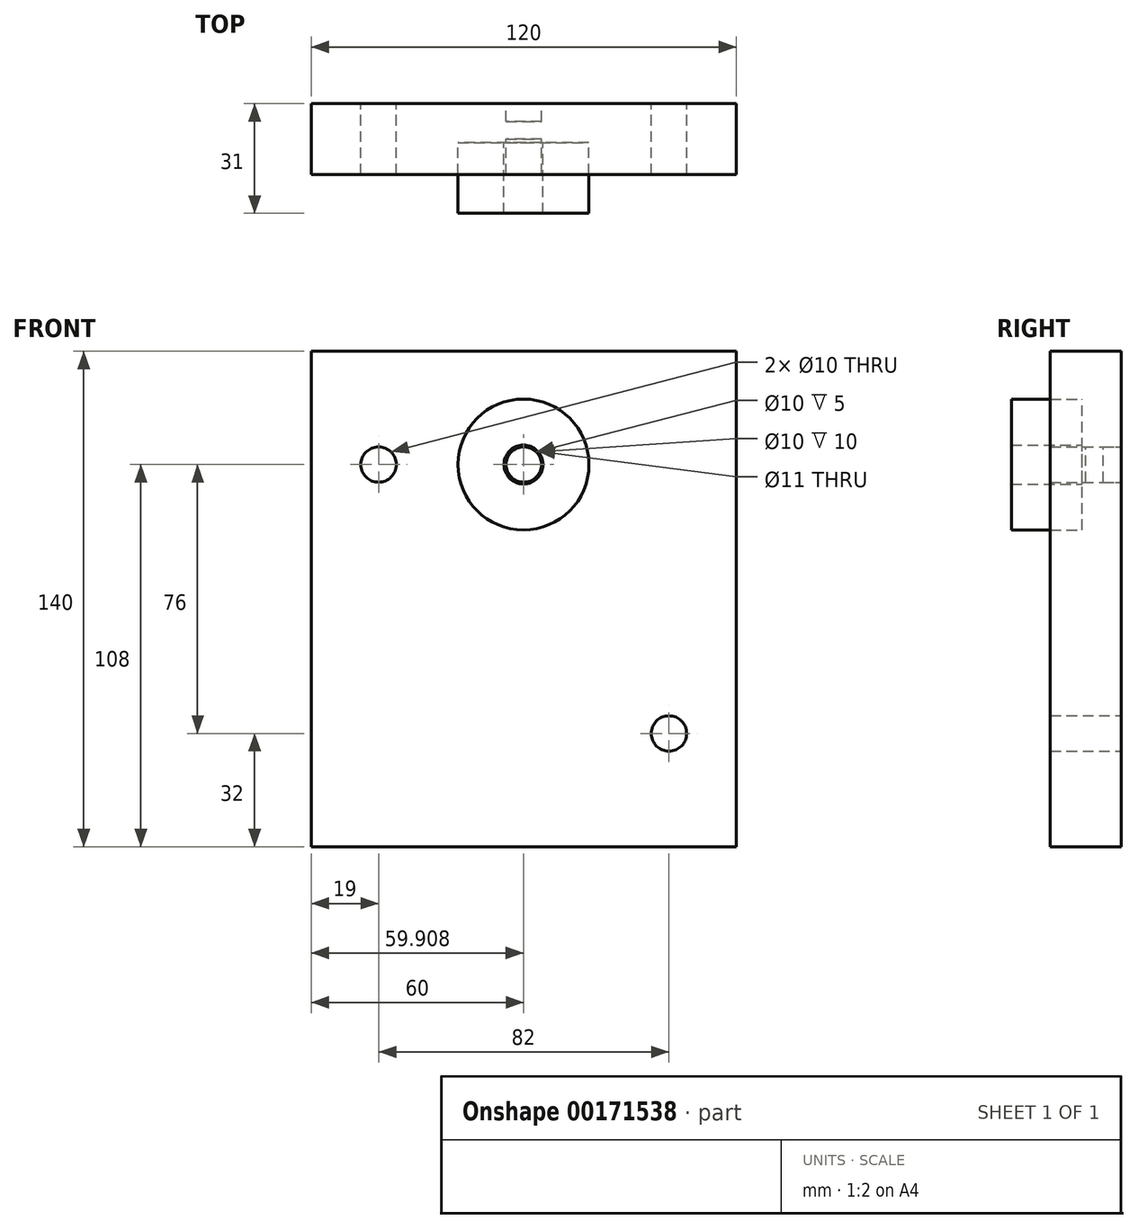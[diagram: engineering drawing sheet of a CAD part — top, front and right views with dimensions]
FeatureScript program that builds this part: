
annotation { "Feature Type Name" : "Feature", "Feature Type Description" : "" }
export const myFeature = defineFeature(function(context is Context, id is Id, definition is map)
    precondition{}
    {
        {
            var Q0;
            Q0=qCreatedBy(makeId("Front.planeOp"),FACE);
            var sketch = newSketch(context, id + "F0", { "sketchPlane" : qUnion([Q0])});
            skLineSegment(sketch, "E0.bottom", {"start": v(60, 70) * mm, "end": v(-60, 70) * mm});
            skLineSegment(sketch, "E0.top", {"start": v(60, -70) * mm, "end": v(-60, -70) * mm});
            skLineSegment(sketch, "E0.left", {"start": v(60, 70) * mm, "end": v(60, -70) * mm});
            skLineSegment(sketch, "E0.right", {"start": v(-60, 70) * mm, "end": v(-60, -70) * mm});
            skPoint(sketch, "E0.middle", {"position": v(0, 0) * mm});
            skLineSegment(sketch, "E1.bottom", {"start": v(60, 19) * mm, "end": v(-60, 19) * mm, "construction": true});
            skLineSegment(sketch, "E1.top", {"start": v(60, -19) * mm, "end": v(-60, -19) * mm, "construction": true});
            skLineSegment(sketch, "E1.left", {"start": v(60, 19) * mm, "end": v(60, -19) * mm, "construction": true});
            skLineSegment(sketch, "E1.right", {"start": v(-60, 17.79) * mm, "end": v(-60, -19) * mm, "construction": true});
            skCircle(sketch, "E2", {"center": v(0, 38) * mm, "radius": 5 * mm});
            skCircle(sketch, "E3", {"center": v(0, -38) * mm, "radius": 5 * mm});
            skCircle(sketch, "E4", {"center": v(0, 38) * mm, "radius": 19 * mm, "construction": true});
            skCircle(sketch, "E5", {"center": v(41, 38) * mm, "radius": 5 * mm});
            skCircle(sketch, "E6.0", {"center": v(41, 38) * mm, "radius": 19 * mm, "construction": true});
            skCircle(sketch, "E7.MirrorC", {"center": v(41, -38) * mm, "radius": 5 * mm});
            skCircle(sketch, "E8.MirrorC", {"center": v(41, -38) * mm, "radius": 19 * mm, "construction": true});
            skCircle(sketch, "E9.MirrorC", {"center": v(-41, 38) * mm, "radius": 5 * mm});
            skCircle(sketch, "E10.MirrorC", {"center": v(-41, 38) * mm, "radius": 19 * mm, "construction": true});
            skCircle(sketch, "E11.MirrorC", {"center": v(-41, -38) * mm, "radius": 5 * mm});
            skCircle(sketch, "E12.MirrorC", {"center": v(-41, -38) * mm, "radius": 19 * mm, "construction": true});
            skSolve(sketch);
        }
        {
            var Q0;
            Q0=qSketchRegion(id+"F0",true);
            var Q1;
            Q1=makeQuery(id+"F0.imprint","IMPRINT",FACE,{"disambiguationData":[TD([[makeQuery(id+"F0.imprint","IMPRINT",EDGE,{"derivedFrom":sQuery(id+"F0.wireOp",EDGE,"E2")}),1.0]])]});
            var Q2;
            Q2=makeQuery(id+"F0.imprint","IMPRINT",FACE,{"disambiguationData":[TD([[makeQuery(id+"F0.imprint","IMPRINT",EDGE,{"derivedFrom":sQuery(id+"F0.wireOp",EDGE,"E9.MirrorC")}),-1.0]])]});
            var Q3;
            Q3=makeQuery(id+"F0.imprint","IMPRINT",FACE,{"disambiguationData":[TD([[makeQuery(id+"F0.imprint","IMPRINT",EDGE,{"derivedFrom":sQuery(id+"F0.wireOp",EDGE,"E5")}),1.0]])]});
            var Q4;
            Q4=makeQuery(id+"F0.imprint","IMPRINT",FACE,{"disambiguationData":[TD([[makeQuery(id+"F0.imprint","IMPRINT",EDGE,{"derivedFrom":sQuery(id+"F0.wireOp",EDGE,"E7.MirrorC")}),-1.0]])]});
            var Q5;
            Q5=makeQuery(id+"F0.imprint","IMPRINT",FACE,{"disambiguationData":[TD([[makeQuery(id+"F0.imprint","IMPRINT",EDGE,{"derivedFrom":sQuery(id+"F0.wireOp",EDGE,"E11.MirrorC")}),1.0]])]});
            extrude(context, id + "F1", {"entities" : qUnion([Q0, Q1, Q2, Q3, Q4, Q5]), "depth" : 10 * mm});
        }
        {
            var Q0;
            Q0=makeQuery(id+"F0.imprint","IMPRINT",FACE,{"disambiguationData":[TD([[makeQuery(id+"F0.imprint","IMPRINT",EDGE,{"derivedFrom":sQuery(id+"F0.wireOp",EDGE,"E2")}),1.0]])]});
            extrude(context, id + "F2", {"entities" : qUnion([Q0]), "operationType" : NewBodyOperationType.REMOVE, "depth" : 5 * mm});
        }
        {
            var Q0;
            Q0=makeQuery(id+"F0.imprint","IMPRINT",FACE,{"disambiguationData":[TD([[makeQuery(id+"F0.imprint","IMPRINT",EDGE,{"derivedFrom":sQuery(id+"F0.wireOp",EDGE,"E9.MirrorC")}),-1.0]])]});
            var Q1;
            Q1=makeQuery(id+"F0.imprint","IMPRINT",FACE,{"disambiguationData":[TD([[makeQuery(id+"F0.imprint","IMPRINT",EDGE,{"derivedFrom":sQuery(id+"F0.wireOp",EDGE,"E11.MirrorC")}),1.0]])]});
            var Q2;
            Q2=makeQuery(id+"F0.imprint","IMPRINT",FACE,{"disambiguationData":[TD([[makeQuery(id+"F0.imprint","IMPRINT",EDGE,{"derivedFrom":sQuery(id+"F0.wireOp",EDGE,"E7.MirrorC")}),-1.0]])]});
            var Q3;
            Q3=makeQuery(id+"F0.imprint","IMPRINT",FACE,{"disambiguationData":[TD([[makeQuery(id+"F0.imprint","IMPRINT",EDGE,{"derivedFrom":sQuery(id+"F0.wireOp",EDGE,"E5")}),1.0]])]});
            var Q4;
            Q4=makeQuery(id+"F0.imprint","IMPRINT",FACE,{"disambiguationData":[TD([[makeQuery(id+"F0.imprint","IMPRINT",EDGE,{"derivedFrom":sQuery(id+"F0.wireOp",EDGE,"E3")}),1.0]])]});
            extrude(context, id + "F3", {"entities" : qUnion([Q0, Q1, Q2, Q3, Q4]), "operationType" : NewBodyOperationType.ADD, "depth" : 20 * mm});
        }
        {
            var Q0;
            Q0=makeQuery(id+"F1.opExtrude","CAP_FACE",FACE,{"disambiguationData":[OSD([sQuery(id+"F0.wireOp",EDGE,"E0.bottom"),sQuery(id+"F0.wireOp",EDGE,"E0.top"),sQuery(id+"F0.wireOp",EDGE,"E0.left"),sQuery(id+"F0.wireOp",EDGE,"E0.right")])],"isStart":false});
            cPlane(context, id + "F4", {"entities" : qUnion([Q0]), "cplaneType" : CPlaneType.OFFSET, "offset" : 1 * mm, "width" : 150 * mm, "height" : 150 * mm});
        }
        {
            var Q0;
            Q0=qCreatedBy(id+"F4.planeOp",FACE);
            var sketch = newSketch(context, id + "F5", { "sketchPlane" : qUnion([Q0])});
            skCircle(sketch, "E13", {"center": v(-0.1, 38) * mm, "radius": 18.5 * mm});
            skCircle(sketch, "E14", {"center": v(-0.1, 38) * mm, "radius": 5.5 * mm});
            skSolve(sketch);
        }
        {
            var Q0;
            Q0=qSketchRegion(id+"F5",true);
            extrude(context, id + "F6", {"entities" : qUnion([Q0]), "depth" : 20 * mm});
        }
    });
